FCSTD DOCUMENT  (FreeCAD 1.0R38641 +468 (Git))
Label: constraints
License: All rights reserved
LicenseURL: https://en.wikipedia.org/wiki/All_rights_reserved
objects: Sketcher::SketchObject×1, PartDesign::Body×1
note: 3 computed .brp shape members not serialized (recipe doc carries the construction recipe); baked Part::Feature solids carry a one-line shape summary decoded from their .brp

FEATURE [Sketcher::SketchObject] Sketch
  ArcFitTolerance = 1e-06
  AttachmentSupport = -> [XY_Plane]
  FullyConstrained = false
  MakeInternals = false
  MapMode = 5
  sketch-geometry (9):
    g0: LineSegment StartX=0 StartY=0 StartZ=0 EndX=100 EndY=0 EndZ=0
    g1: LineSegment StartX=100 StartY=0 StartZ=0 EndX=100 EndY=100 EndZ=0
    g2: LineSegment StartX=100 StartY=100 StartZ=0 EndX=0 EndY=100 EndZ=0
    g3: LineSegment StartX=0 StartY=100 StartZ=0 EndX=0 EndY=0 EndZ=0
    g4: LineSegment StartX=50 StartY=100 StartZ=0 EndX=50 EndY=0 EndZ=0
    g5: LineSegment StartX=0 StartY=50 StartZ=0 EndX=100 EndY=50 EndZ=0
    g6: Circle CenterX=22.0979 CenterY=61.8756 CenterZ=0 NormalX=0 NormalY=0 NormalZ=1 AngleXU=0 Radius=5
    g7: Circle CenterX=77.9021 CenterY=61.8756 CenterZ=0 NormalX=0 NormalY=0 NormalZ=1 AngleXU=0 Radius=5
    g8: Circle CenterX=77.9021 CenterY=38.1244 CenterZ=0 NormalX=0 NormalY=0 NormalZ=1 AngleXU=0 Radius=5
  constraints (20):
    c: Coincident(g0,g1)
    c: Coincident(g1,g2)
    c: Coincident(g2,g3)
    c: Coincident(g3,g0)
    c: Horizontal(g0)
    c: Horizontal(g2)
    c: Vertical(g1)
    c: Vertical(g3)
    c: Distance(g1,g3) = 100
    c: Distance(g0,g2) = 100
    c: Coincident(g0,g-1)
    c: Symmetric(g2,g2,g4)
    c: Symmetric(g0,g0,g4)
    c: Symmetric(g1,g0,g5)
    c: Symmetric(g0,g2,g5)
    c: Diameter(g6) = 10
    c: Diameter(g7) = 10
    c: Diameter(g8) = 10
    c: Symmetric(g6,g7,g4)
    c: Symmetric(g8,g7,g5)
FEATURE [PartDesign::Body] Body
  AllowCompound = false
  Group = -> [Sketch]
  Origin = -> Origin
